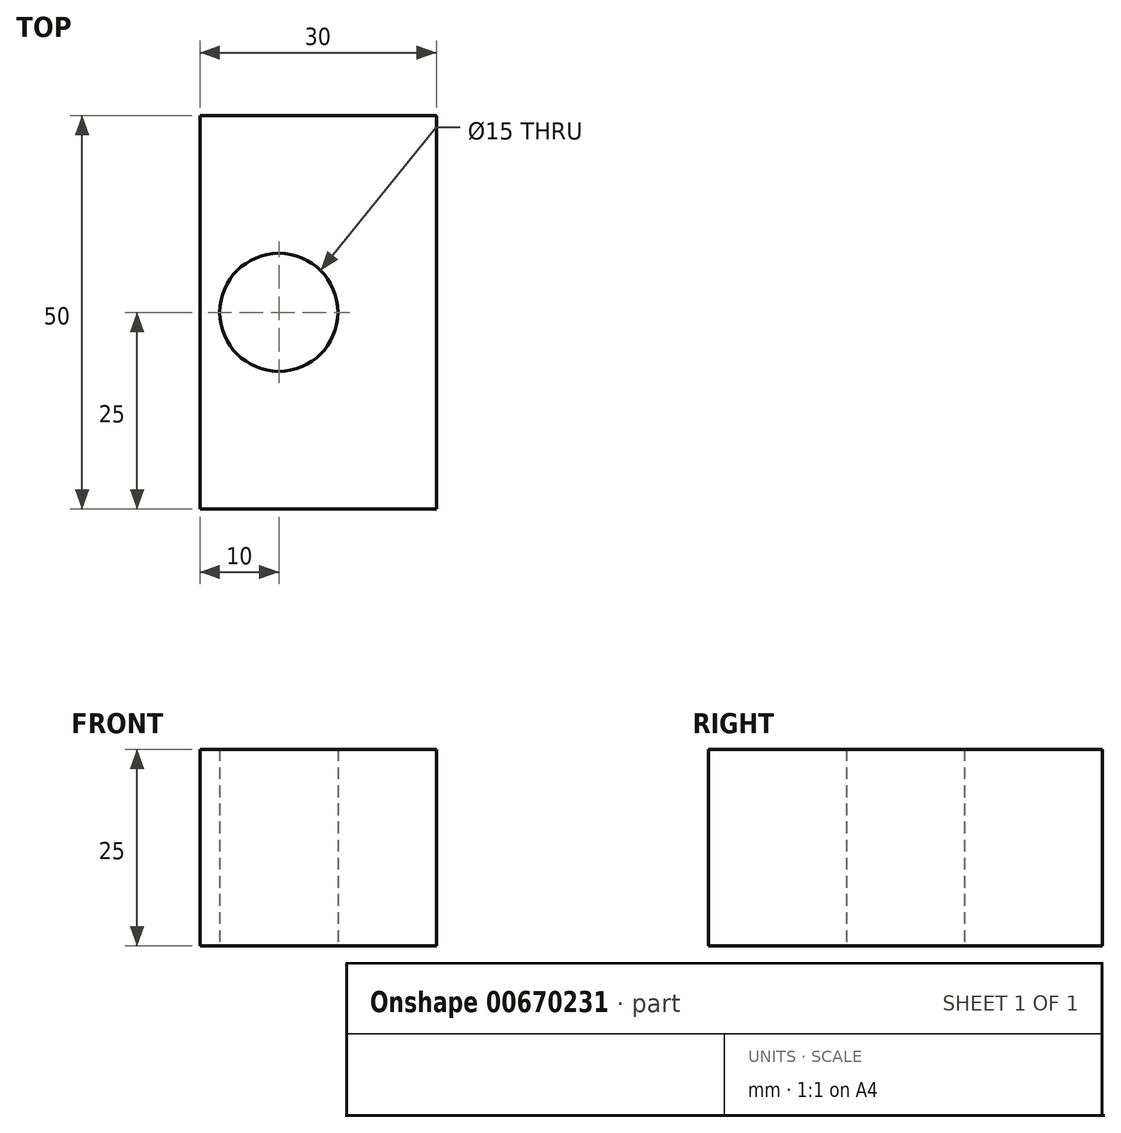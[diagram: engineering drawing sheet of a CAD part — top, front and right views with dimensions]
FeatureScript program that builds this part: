
annotation { "Feature Type Name" : "Feature", "Feature Type Description" : "" }
export const myFeature = defineFeature(function(context is Context, id is Id, definition is map)
    precondition{}
    {
        {
            var Q0;
            Q0=qCreatedBy(makeId("Top.planeOp"),FACE);
            var sketch = newSketch(context, id + "F0", { "sketchPlane" : qUnion([Q0])});
            skLineSegment(sketch, "E0.bottom", {"start": v(-10, 25) * mm, "end": v(20, 25) * mm});
            skLineSegment(sketch, "E0.top", {"start": v(-10, -25) * mm, "end": v(20, -25) * mm});
            skLineSegment(sketch, "E0.left", {"start": v(-10, 25) * mm, "end": v(-10, -25) * mm});
            skLineSegment(sketch, "E0.right", {"start": v(20, 25) * mm, "end": v(20, -25) * mm});
            skCircle(sketch, "E1", {"center": v(0, 0) * mm, "radius": 7.5 * mm});
            skSolve(sketch);
        }
        {
            var Q0;
            Q0=makeQuery(id+"F0.imprint","IMPRINT",FACE,{"disambiguationData":[TD([[makeQuery(id+"F0.imprint","IMPRINT",EDGE,{"derivedFrom":sQuery(id+"F0.wireOp",EDGE,"E0.bottom")}),-1.0]])]});
            extrude(context, id + "F1", {"entities" : qUnion([Q0]), "depth" : 25 * mm, "offsetDistance" : 25 * mm});
        }
    });
